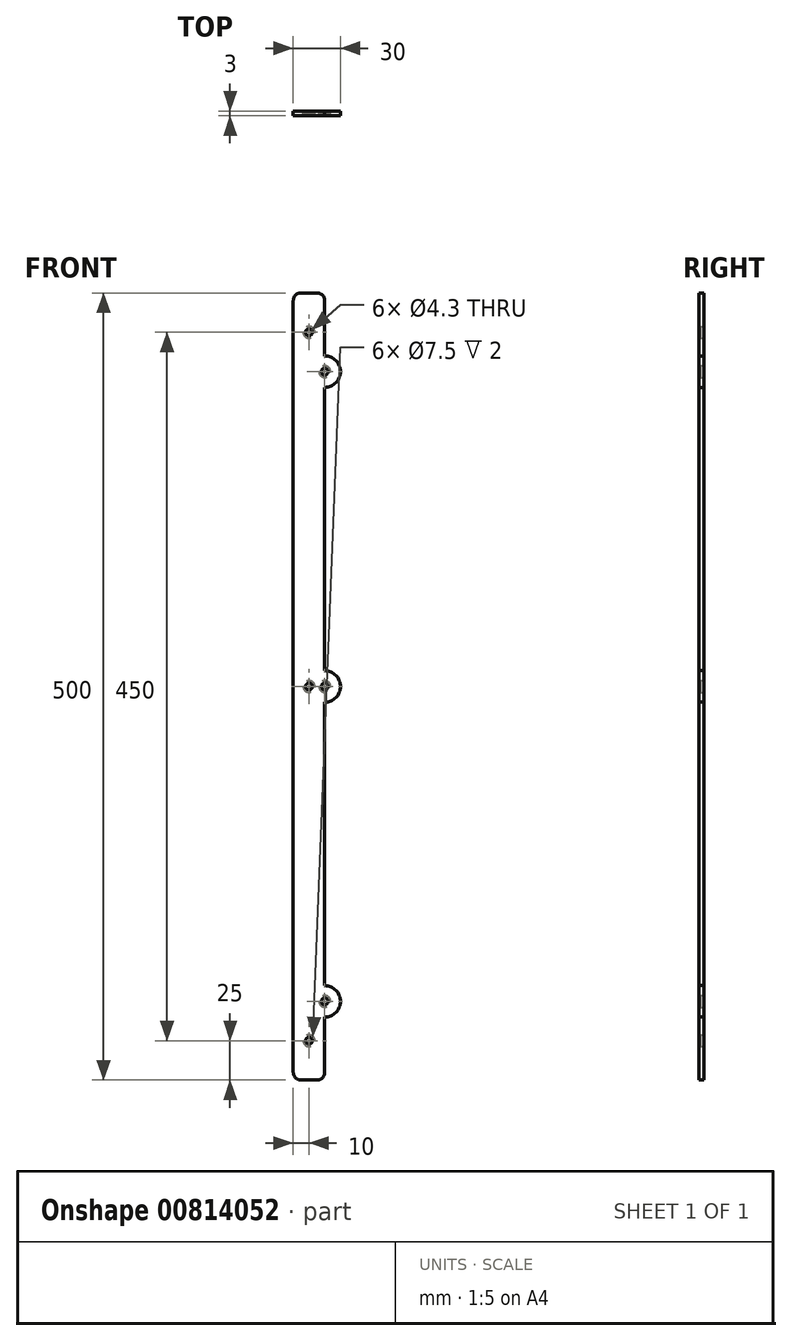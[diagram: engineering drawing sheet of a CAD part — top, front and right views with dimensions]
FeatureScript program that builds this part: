
annotation { "Feature Type Name" : "Feature", "Feature Type Description" : "" }
export const myFeature = defineFeature(function(context is Context, id is Id, definition is map)
    precondition{}
    {
        {
            var Q0;
            Q0=qCreatedBy(makeId("Front.planeOp"),FACE);
            var sketch = newSketch(context, id + "F0", { "sketchPlane" : qUnion([Q0])});
            skLineSegment(sketch, "E0.bottom", {"start": v(-10, 250) * mm, "end": v(10, 250) * mm});
            skLineSegment(sketch, "E0.top", {"start": v(-10, -250) * mm, "end": v(10, -250) * mm});
            skLineSegment(sketch, "E0.left", {"start": v(-10, 250) * mm, "end": v(-10, -250) * mm});
            skLineSegment(sketch, "E0.right", {"start": v(10, 250) * mm, "end": v(10, -250) * mm});
            skPoint(sketch, "E0.middle", {"position": v(0, 0) * mm});
            skCircle(sketch, "E1", {"center": v(10, 0) * mm, "radius": 10 * mm});
            skCircle(sketch, "E2", {"center": v(10, 200) * mm, "radius": 10 * mm});
            skCircle(sketch, "E3", {"center": v(10, -200) * mm, "radius": 10 * mm});
            skLineSegment(sketch, "E4", {"start": v(20, 0) * mm, "end": v(20, 200) * mm, "construction": true});
            skLineSegment(sketch, "E5", {"start": v(0, 250) * mm, "end": v(0, -250) * mm, "construction": true});
            skPoint(sketch, "E6", {"position": v(0, 225) * mm});
            skPoint(sketch, "E7.MirrorP", {"position": v(0, -225) * mm});
            skSolve(sketch);
        }
        {
            var Q0;
            Q0 = qSketchRegion(id + "F0", true);
            extrude(context, id + "F1", {"entities" : qUnion([Q0]), "depth" : 3 * mm, "offsetDistance" : 25 * mm});
        }
        {
            var Q0;
            Q0=sQuery(id+"F0.wireOp",VERTEX,"E0.middle");
            var Q1;
            Q1=sQuery(id+"F0.wireOp",VERTEX,"E6");
            var Q2;
            Q2=sQuery(id+"F0.wireOp",VERTEX,"E7.MirrorP");
            var Q3;
            Q3=makeQuery(id+"F1.opExtrude","SWEPT_BODY",BODY,{"disambiguationData":[OSD([sQuery(id+"F0.wireOp",EDGE,"E0.bottom"),sQuery(id+"F0.wireOp",EDGE,"E0.top"),sQuery(id+"F0.wireOp",EDGE,"E0.left"),sQuery(id+"F0.wireOp",EDGE,"E0.right"),sQuery(id+"F0.wireOp",EDGE,"zQk7otoN-bbNb-79Ht-lchy-IMR8xu7S5Ae9"),sQuery(id+"F0.wireOp",EDGE,"f95163ac-d509-4446-88d7-1ecb5150997e0.MirrorC"),sQuery(id+"F0.wireOp",EDGE,"7b545a5b-be98-458e-90bc-1e96104b5c72.MirrorC"),sQuery(id+"F0.wireOp",EDGE,"E1"),sQuery(id+"F0.wireOp",EDGE,"E2"),sQuery(id+"F0.wireOp",EDGE,"E3")])]});
            hole(context, id + "F2", {"style" : HoleStyle.C_BORE, "endStyle" : HoleEndStyle.THROUGH, "oppositeDirection" : true, "holeDiameter" : 4.3 * mm, "cBoreDiameter" : 7.5 * mm, "cBoreDepth" : 2 * mm, "majorDiameter" : 5 * mm, "isTappedThrough" : true, "tappedDepth" : 12 * mm, "tapClearance" : 3, "startFromSketch" : true, "locations" : qUnion([Q0, Q1, Q2]), "scope" : qUnion([Q3])});
        }
        {
            var Q0;
            Q0=sQuery(id+"F0.wireOp",VERTEX,"E1.center");
            var Q1;
            Q1=sQuery(id+"F0.wireOp",VERTEX,"E2.center");
            var Q2;
            Q2=sQuery(id+"F0.wireOp",VERTEX,"E3.center");
            var Q3;
            Q3=makeQuery(id+"F1.opExtrude","SWEPT_BODY",BODY,{"disambiguationData":[OSD([sQuery(id+"F0.wireOp",EDGE,"E0.bottom"),sQuery(id+"F0.wireOp",EDGE,"E0.top"),sQuery(id+"F0.wireOp",EDGE,"E0.left"),sQuery(id+"F0.wireOp",EDGE,"E0.right"),sQuery(id+"F0.wireOp",EDGE,"E1"),sQuery(id+"F0.wireOp",EDGE,"E2"),sQuery(id+"F0.wireOp",EDGE,"E3")])]});
            hole(context, id + "F3", {"style" : HoleStyle.C_BORE, "endStyle" : HoleEndStyle.THROUGH, "oppositeDirection" : true, "holeDiameter" : 4.3 * mm, "cBoreDiameter" : 7.5 * mm, "cBoreDepth" : 2 * mm, "majorDiameter" : 5 * mm, "isTappedThrough" : true, "tappedDepth" : 12 * mm, "tapClearance" : 3, "locations" : qUnion([Q0, Q1, Q2]), "scope" : qUnion([Q3])});
        }
        {
            var Q0;
            Q0=makeQuery(id+"F1.opExtrude","SWEPT_EDGE",EDGE,{"disambiguationData":[OSD([sQuery(id+"F0.wireOp",EDGE,"E0.bottom"),sQuery(id+"F0.wireOp",EDGE,"E0.left")])]});
            var Q1;
            Q1=makeQuery(id+"F1.opExtrude","SWEPT_EDGE",EDGE,{"disambiguationData":[OSD([sQuery(id+"F0.wireOp",EDGE,"E0.bottom"),sQuery(id+"F0.wireOp",EDGE,"E0.right")])]});
            var Q2;
            Q2=makeQuery(id+"F1.opExtrude","SWEPT_EDGE",EDGE,{"disambiguationData":[OSD([sQuery(id+"F0.wireOp",EDGE,"E0.top"),sQuery(id+"F0.wireOp",EDGE,"E0.left")])]});
            var Q3;
            Q3=makeQuery(id+"F1.opExtrude","SWEPT_EDGE",EDGE,{"disambiguationData":[OSD([sQuery(id+"F0.wireOp",EDGE,"E0.top"),sQuery(id+"F0.wireOp",EDGE,"E0.right")])]});
            fillet(context, id + "F4", {"entities" : qUnion([Q0, Q1, Q2, Q3]), "radius" : 5 * mm, "tangentPropagation" : true, "allowEdgeOverflow" : false});
        }
    });
